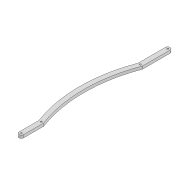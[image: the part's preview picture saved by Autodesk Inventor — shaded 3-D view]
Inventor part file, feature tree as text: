
AUTODESK INVENTOR PART (.ipt)
format: ipt  version: 2022 (Build 260153000, 153)  size: 107,008 bytes
history: native  units: mm
features: extrude x1, sketch x1
ambient origin geometry x8: Origin, YZ Plane, XZ Plane, XY Plane, X Axis, Y Axis, Z Axis, Center Point
bodies: Solid1 (feature_tree)
feature tree (2):
  extrude  "Extrusion1"  Depth=300.0mm
  sketch  "Sketch1"  dims[d0=3.3mm d1=3.3mm d2=10.0mm d3=312.648mm d6=6.0mm d7=0.0mm d10=3.3mm d11=42.6mm d12=3.3mm d13=254.274mm d16=300.0mm d17=300.0mm]
